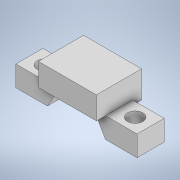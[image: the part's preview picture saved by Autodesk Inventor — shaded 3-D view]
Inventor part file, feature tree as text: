
AUTODESK INVENTOR PART (.ipt)
format: ipt  version: 2020.2 (Build 242310000, 310)  size: 155,648 bytes
history: native  units: mm
features: sketch x4, extrude x3, hole x1
ambient origin geometry x8: Origin, YZ Plane, XZ Plane, XY Plane, X Axis, Y Axis, Z Axis, Center Point
bodies: Solid1 (feature_tree)
feature tree (8):
  extrude  "Extrusion1"  Depth=6.4135mm
  extrude  "Extrusion2"  Depth=6.4262mm
  hole  "Hole2"  [1 undecoded]
  extrude  "Extrusion3"  Depth=5.0mm
  sketch  "Sketch1"  dims[d0=6.4135mm d1=6.4262mm]
  sketch  "Sketch3"  dims[d2=60.0deg d3=6.4262mm]
  sketch  "Sketch4"  dims[d4=120.0deg d5=6.4262mm]
  sketch  "Sketch5"  dims[d6=120.0deg d7=6.4262mm d8=120.0deg d9=6.4262mm d10=120.0deg d11=7.0mm d12=180.0deg d13=4.0mm d15=5.0mm d16=7.0mm d17=7.0mm d18=6.0mm d19=0.0mm d20=7.0mm d30=6.0mm d31=2.0mm d32=0.0mm d36=10.0mm d37=20.0mm d38=0.0mm d39=3.4mm d40=6.0mm d41=6.3mm d42=5.0mm d43=90.0deg d44=8.0mm d45=20.594885mm d46=2.0mm d47=5.0mm d48=0.0mm]
note: 1 required parameter value undecoded (feature->parameter linkage not recoverable at this tier; creation-order binding heuristic only, values carry confidence <= 0.55)
